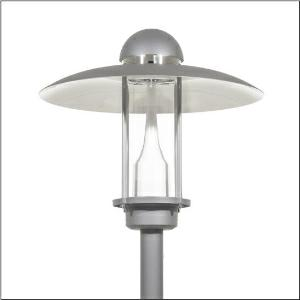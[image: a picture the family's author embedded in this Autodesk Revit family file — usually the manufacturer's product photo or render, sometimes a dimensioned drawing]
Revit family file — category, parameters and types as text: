
# Revit family: city-light_elegance_iq___st1_2a_5xa5265kf14h_1fe5
name_source: partatom
category: Lighting Fixtures
units: mm (PartAtom-declared; Revit-internal decimal feet)

## family parameters
Cut with Voids When Loaded = No
Host = Face
Light Source = No
Part Type = Normal
Room Calculation Point = No
Round Connector Dimension = Use Diameter
Shared = No

## types (1)
- --- (1 x LED, 1470 lm, 10 W, 4000K)
    Apparent Load = 10 VA
    CIE Flux Codes = 22 62 94 98 100
    Color Rendering = 70
    Color Temperature = 4000K
    Default Elevation = 1800 mm
    Description = City-Light Elegance iQ, mast luminaire, Module 540 iQ-SR, primary light control with 3 zone facetted reflector, of plastic, silver coated, highly specular, structured, primary optical cover: cover, of PMMA, transparent, light distribution: ST1.2a, light emission: direct distribution, primary light characteristic: asymmetric, installation type: post-top, LED, High Power LED, rated luminous flux: 1.470lm, luminous efficacy: 147lm/W, light colour: 740, colour temperature: 4000K, control gear: ECG iQ, control: presetting dimming logarithmic, Street-Remote, Auto-Match, Temp-Guard, Lumen-Switch, Night-Set, Smart-Wire, Light-Fading, Desk-Remote (wireless, voltage-free reading and setting of iQ features in the workshop via application-optimized NFC function/RFID function), optimised constant luminous flux control (CLO 2.0), with terminal, 6-pole, max. 2.5mm², mains connection: 230..240V, AC, 50/60Hz, start of lifetime: 10W, end of service life: 10W, reduction: 5W, luminaire housing, upper part, of aluminium, coated, Siteco® metallic grey (DB 702S), diameter: 750mm, height: 675mm, spigot size: d x l = 76 x 70mm (post-top) | with reducer (optional accessory) 60 x 70mm, post-top mast mounting element, of diecast aluminium, coated, Siteco® metallic grey (DB 702S), Module 540 iQ-SR, traffic white (RAL 9016), equipment: standard, protection rating (complete): IP65, insulation class (complete): insulation class II (safety insulation), certification: CE, ENEC, VDE, packaging unit: 1 piece

Light Distribution: ST1.2a
    Height = 675 mm
    Lamp = 1 x LED
    Lamp Light Flux = 1470 lm
    Lamp Power = 10 W
    Lamp count = 1
    Length = 750 mm
    Luminous efficacy = 147 lm/W
    Manufacturer = Siteco
    ModVariant = No
    Model = 5XA5265KF14H
    Number of Poles = 1
    OnlyDefault = Yes
    Power Factor = 1
    Product Name = City-Light Elegance iQ | ST1.2a
    Product group = mast luminaire | pylon top
    ProductGroupID = 6100
    Protection Class = Protection class II
    Protection Degree = IP 65
    RLX_Detail_Level = 1
    RLX_Emergency_Light_Flux = 0 lm
    RLX_Emergency_Type = 0
    RLX_Emergency_Type_DB = No
    RlxData = <blob elided: 103941 chars, md5=b5d3559c>
    Socket = socket
    Standby Power = 0 W
    System Light Flux = 1470 lm
    System Power = 10 W
    Type Comments = factory setting: luminous flux: 100 % | dim-lin: 254 | 401 mA
    Type Image = l_1006912.jpg
    URL = http://relux.com
    VarID = @adj_109999
    Voltage = 0 V
    Weight = 0.00 kg
    Width = 0 mm  [stored 0 ft]

note: [stored X ft] marks values corroborated as IEEE doubles in the binary element streams (Revit-internal decimal feet)

## geometry (parser evidence)
native form markers: Blend x4, Sweep x8
no freeform markers — native parametric forms only
